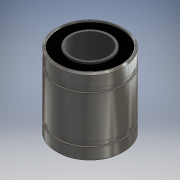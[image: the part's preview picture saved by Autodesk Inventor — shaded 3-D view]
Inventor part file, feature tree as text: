
AUTODESK INVENTOR PART (.ipt)
format: ipt  version: 2016 (Build 200138000, 138)  size: 181,760 bytes
history: native  units: mm
features: sketch x6, extrude x5, other x2, hole x1, chamfer x1
ambient origin geometry x8: Origin, YZ Plane, XZ Plane, XY Plane, X Axis, Y Axis, Z Axis, Center Point
bodies: Body1 (feature_tree)
feature tree (15):
  extrude  "Выдавливание2"  Depth=15.0mm
  hole  "Отверстие1"  [1 undecoded]
  other  "РабПлоскость1"
  other  "РабПлоскость2"
  sketch  "Эскиз10"
  extrude  "Выдавливание3"  [1 undecoded]
  extrude  "Выдавливание4"  [1 undecoded]
  extrude  "Выдавливание5"  Depth=14.3mm
  extrude  "Выдавливание6"  Depth=15.0mm
  chamfer  "Фаска1"  Distance=14.3mm
  sketch  "Эскиз6"
  sketch  "Эскиз8"
  sketch  "Эскиз11"
  sketch  "Эскиз12"
  sketch  "Эскиз13"
note: 3 required parameter values undecoded (feature->parameter linkage not recoverable at this tier; creation-order binding heuristic only, values carry confidence <= 0.55)
